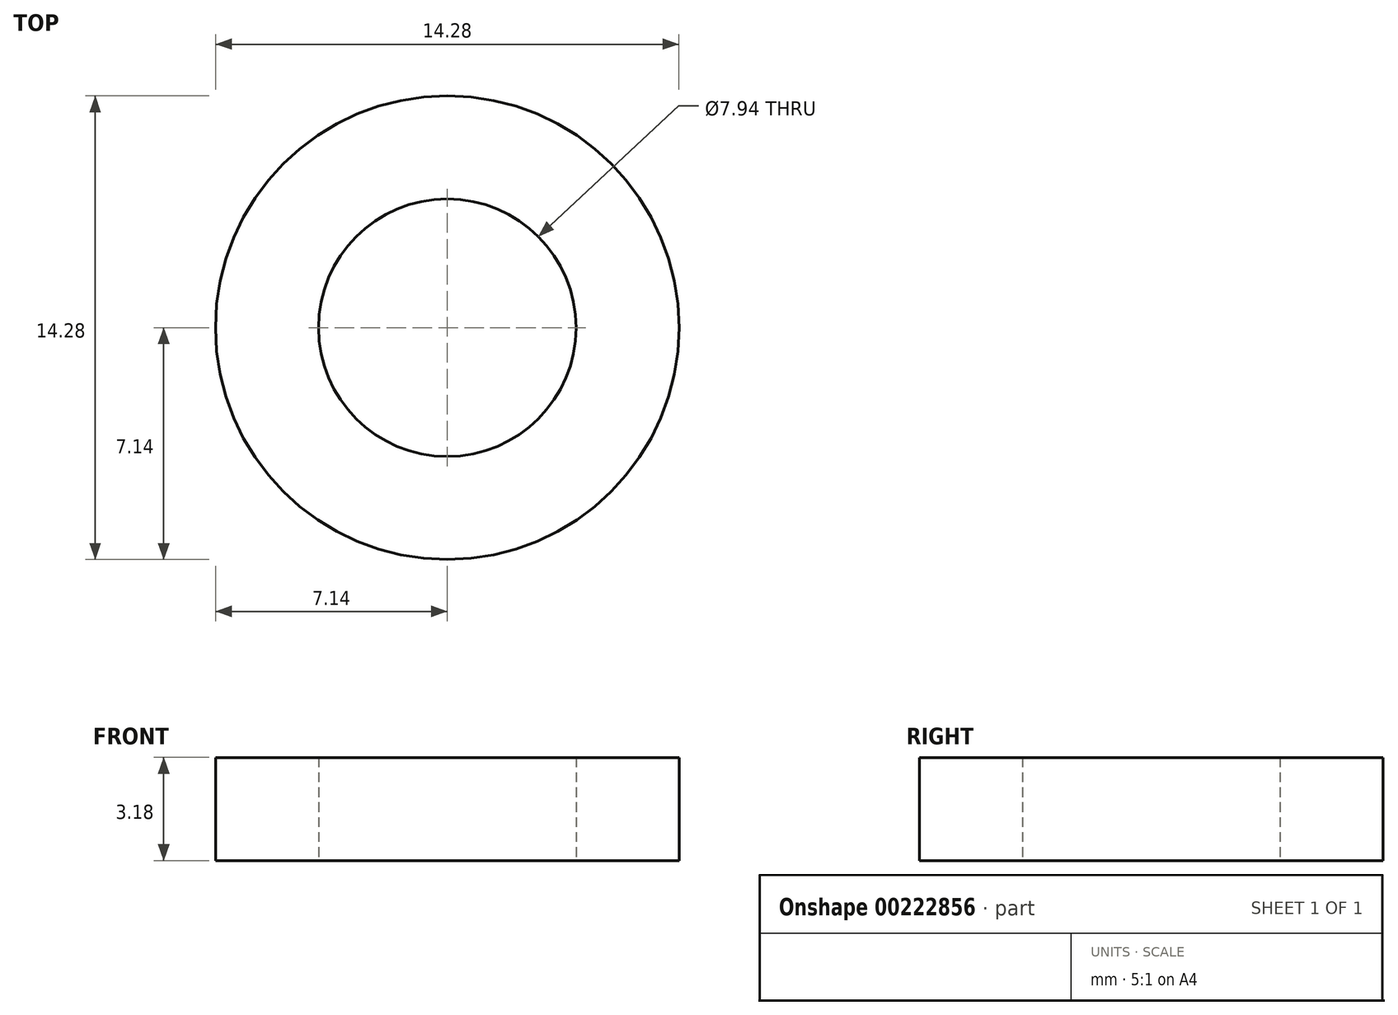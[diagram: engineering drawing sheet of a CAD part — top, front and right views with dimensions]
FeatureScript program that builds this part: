
annotation { "Feature Type Name" : "Feature", "Feature Type Description" : "" }
export const myFeature = defineFeature(function(context is Context, id is Id, definition is map)
    precondition{}
    {
        {
            var Q0;
            Q0=qCreatedBy(makeId("Top.planeOp"),FACE);
            var sketch = newSketch(context, id + "F0", { "sketchPlane" : qUnion([Q0])});
            skCircle(sketch, "E0", {"center": v(0, 0) * mm, "radius": 7.14 * mm});
            skCircle(sketch, "E1", {"center": v(0, 0) * mm, "radius": 3.97 * mm});
            skSolve(sketch);
        }
        {
            var Q0;
            Q0 = qSketchRegion(id + "F0", true);
            extrude(context, id + "F1", {"entities" : qUnion([Q0]), "depth" : 3.17 * mm});
        }
    });
